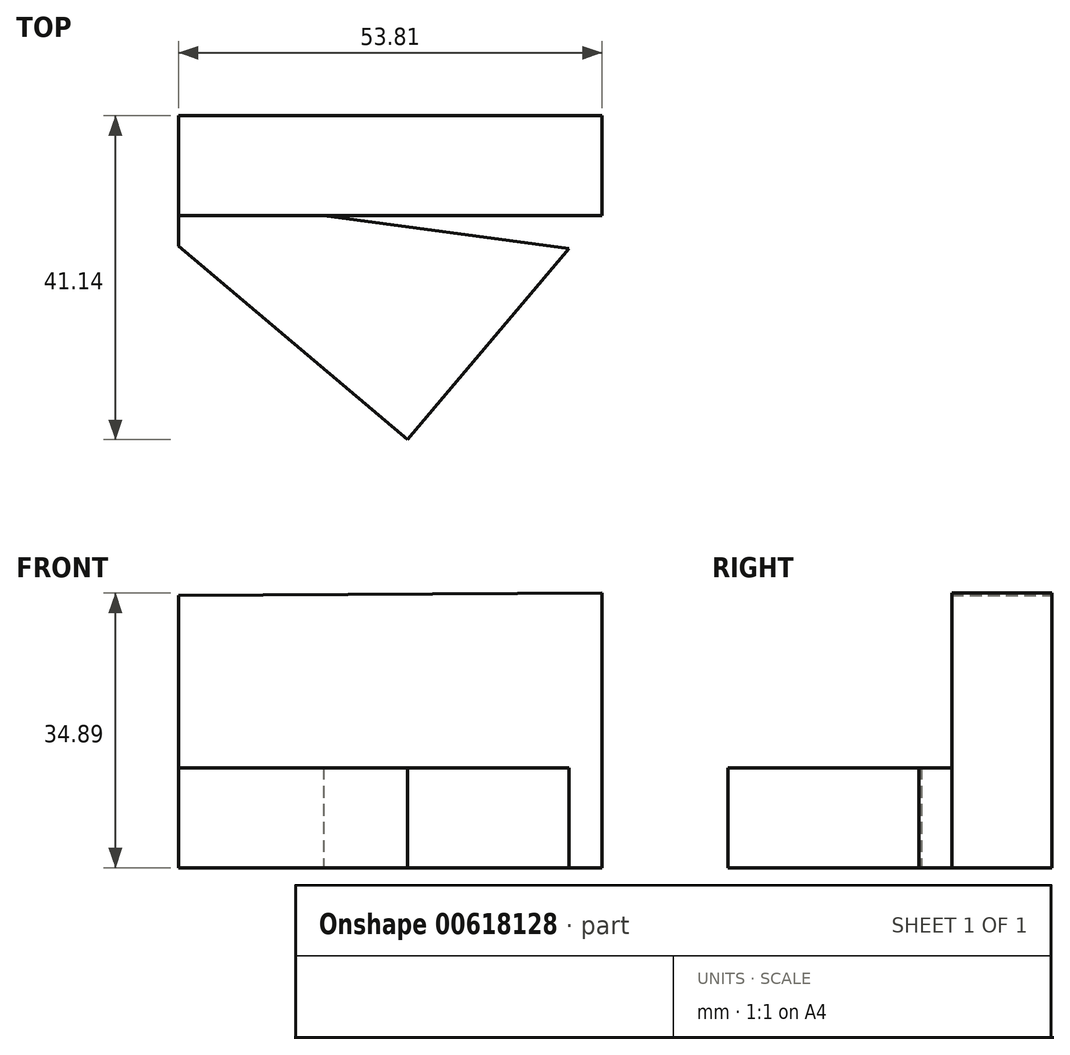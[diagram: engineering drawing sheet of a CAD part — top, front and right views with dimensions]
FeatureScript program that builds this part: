
annotation { "Feature Type Name" : "Feature", "Feature Type Description" : "" }
export const myFeature = defineFeature(function(context is Context, id is Id, definition is map)
    precondition{}
    {
        {
            var Q0;
            Q0=qCreatedBy(makeId("Front.planeOp"),FACE);
            var sketch = newSketch(context, id + "F0", { "sketchPlane" : qUnion([Q0])});
            skLineSegment(sketch, "E0", {"start": v(0, 34.58) * mm, "end": v(0, 0) * mm});
            skLineSegment(sketch, "E1", {"start": v(0, 0) * mm, "end": v(53.8, 0) * mm});
            skLineSegment(sketch, "E2", {"start": v(53.8, 0) * mm, "end": v(53.8, 34.89) * mm});
            skLineSegment(sketch, "E3", {"start": v(53.8, 34.89) * mm, "end": v(0, 34.58) * mm});
            skSolve(sketch);
        }
        {
            var Q0;
            Q0=makeQuery(id+"F0.imprint","IMPRINT",FACE,{"disambiguationData":[TD([[makeQuery(id+"F0.imprint","IMPRINT",EDGE,{"derivedFrom":sQuery(id+"F0.wireOp",EDGE,"E0")}),1.0]])]});
            extrude(context, id + "F1", {"entities" : qUnion([Q0]), "depth" : 12.7 * mm, "offsetDistance" : 25.4 * mm});
        }
        {
            var Q0;
            Q0=qCreatedBy(makeId("Top.planeOp"),FACE);
            var sketch = newSketch(context, id + "F2", { "sketchPlane" : qUnion([Q0])});
            skLineSegment(sketch, "E4", {"start": v(0, -10.23) * mm, "end": v(0, -16.58) * mm});
            skLineSegment(sketch, "E5", {"start": v(0, -16.58) * mm, "end": v(29.12, -41.14) * mm});
            skLineSegment(sketch, "E6", {"start": v(29.12, -41.14) * mm, "end": v(49.6, -16.87) * mm});
            skLineSegment(sketch, "E7", {"start": v(49.6, -16.87) * mm, "end": v(0, -10.23) * mm});
            skSolve(sketch);
        }
        {
            var Q0;
            Q0=makeQuery(id+"F2.imprint","IMPRINT",FACE,{"disambiguationData":[TD([[makeQuery(id+"F2.imprint","IMPRINT",EDGE,{"derivedFrom":sQuery(id+"F2.wireOp",EDGE,"E4")}),1.0]])]});
            extrude(context, id + "F3", {"entities" : qUnion([Q0]), "operationType" : NewBodyOperationType.ADD, "depth" : 12.7 * mm, "offsetDistance" : 25.4 * mm});
        }
    });
